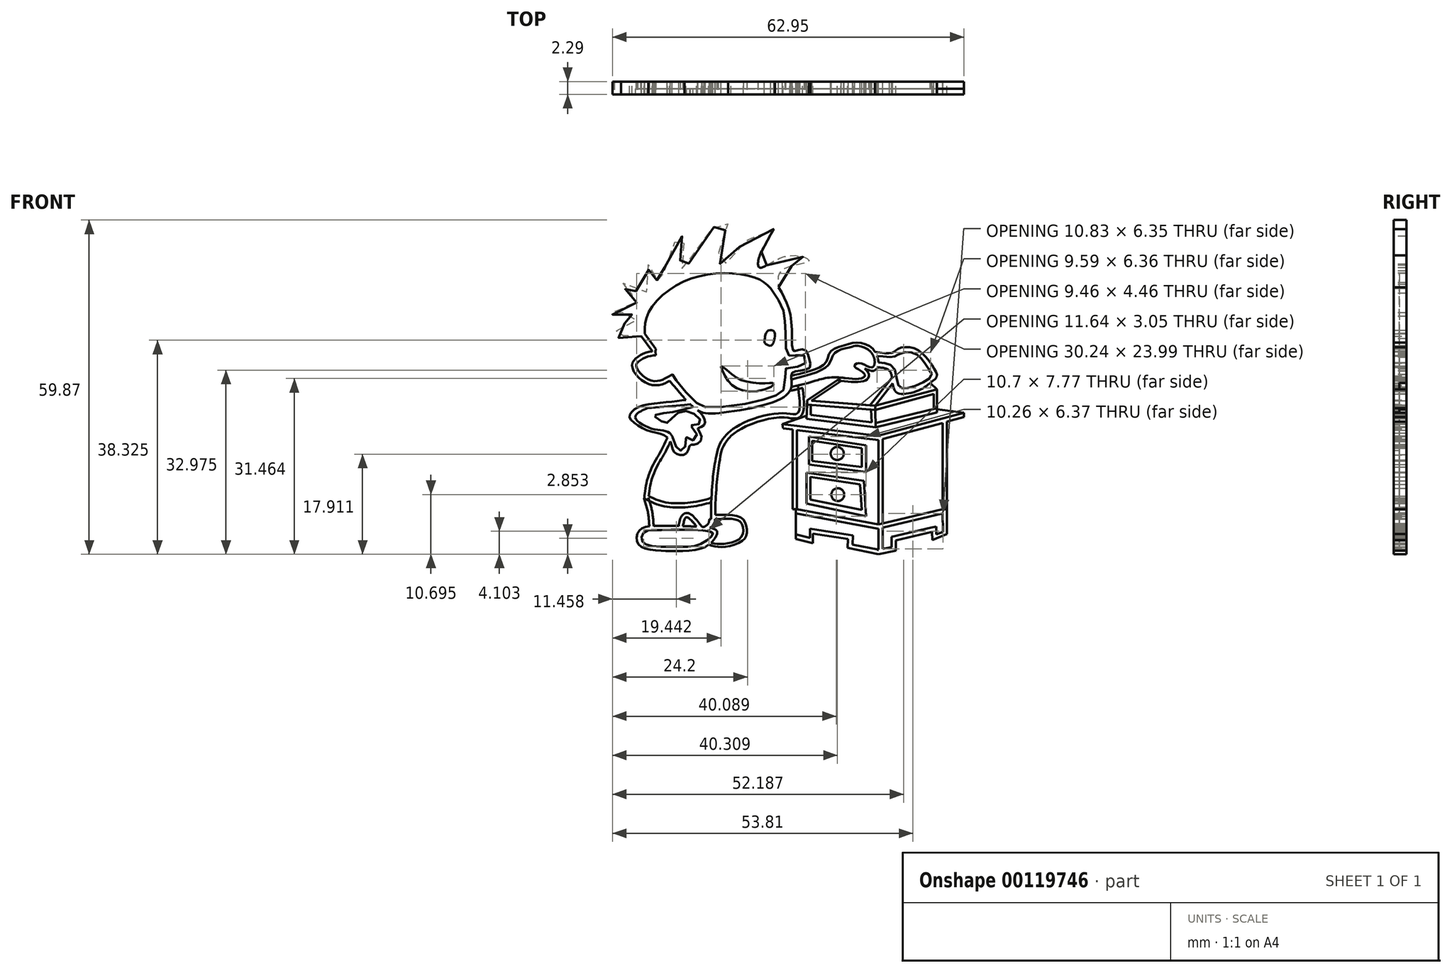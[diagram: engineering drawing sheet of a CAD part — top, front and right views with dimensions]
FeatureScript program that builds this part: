
annotation { "Feature Type Name" : "Feature", "Feature Type Description" : "" }
export const myFeature = defineFeature(function(context is Context, id is Id, definition is map)
    precondition{}
    {
        {
            var Q0;
            Q0=qCreatedBy(makeId("Front.planeOp"),FACE);
            var sketch = newSketch(context, id + "F0", { "sketchPlane" : qUnion([Q0])});
            skFitSpline(sketch, "E0", {"points": [v(200.47, 7.48) * mm, v(198.73, 7.17) * mm, v(197.12, 6.3) * mm, v(196.3, 5.12) * mm, v(196.99, 3.25) * mm, v(199.43, 1.5) * mm, v(201.65, 1.5) * mm, v(203.03, 2.15) * mm], "startDerivative": vector(-12.85, -1.34) * mm, "endDerivative": vector(9.7, 5.6) * mm});
            skFitSpline(sketch, "E1", {"points": [v(220.12, 1.68) * mm, v(216.68, 2.03) * mm, v(214.2, 3.29) * mm, v(212.24, 4.78) * mm, v(212.85, 3.16) * mm, v(214.76, 0.99) * mm, v(218.9, 0.29) * mm, v(221.69, 1.5) * mm, v(221.43, 1.73) * mm, v(220.12, 1.68) * mm]});
            skFitSpline(sketch, "E2", {"points": [v(222.53, 18.87) * mm, v(224.03, 16) * mm, v(224.88, 11.69) * mm, v(225.14, 7.57) * mm, v(225.8, 7.57) * mm, v(227.23, 7.7) * mm, v(228.08, 5.88) * mm, v(227.95, 4.38) * mm, v(225.53, 3.85) * mm, v(224.82, 3.29) * mm, v(224.82, 1.05) * mm, v(222.2, -1.43) * mm, v(211.57, -3.65) * mm, v(208.04, -3.13) * mm, v(203.03, 2.15) * mm], "startDerivative": vector(22.12, -37.26) * mm, "endDerivative": vector(-48.02, 59.15) * mm});
            skFitSpline(sketch, "E3", {"points": [v(197.92, 10.15) * mm, v(195.7, 10.54) * mm, v(193.15, 9.76) * mm, v(194.66, 12.3) * mm, v(197.27, 13.15) * mm, v(194.92, 14.33) * mm, v(192.83, 13.74) * mm, v(193.94, 15.63) * mm, v(197.79, 16.28) * mm, v(195.05, 18.57) * mm, v(194.4, 19.74) * mm, v(198.73, 17.92) * mm, v(199.22, 23) * mm, v(200.53, 20.6) * mm, v(201.5, 19.42) * mm, v(202.94, 25.49) * mm, v(205.62, 27.97) * mm, v(204.9, 23.6) * mm, v(205.75, 21.83) * mm, v(207.7, 26.14) * mm, v(213.39, 30.9) * mm, v(211.89, 26.01) * mm, v(212.4, 22.81) * mm, v(216.2, 26.8) * mm, v(221.8, 29.2) * mm, v(219.65, 25.68) * mm, v(219.13, 22.42) * mm, v(224.1, 24.5) * mm, v(227.94, 23.6) * mm, v(223.24, 22.03) * mm, v(222.53, 18.87) * mm], "startDerivative": vector(-75.72, 34.65) * mm, "endDerivative": vector(13.75, -116.93) * mm});
            skLineSegment(sketch, "E4", {"start": v(197.92, 10.15) * mm, "end": v(199.89, 7.42) * mm});
            skFitSpline(sketch, "E5", {"points": [v(221.8, 10.83) * mm, v(220.92, 11.22) * mm, v(220.23, 10.63) * mm, v(220.04, 9.66) * mm, v(220.04, 8.97) * mm, v(221.17, 8.44) * mm, v(221.7, 9.36) * mm, v(221.8, 10.83) * mm]});
            skFitSpline(sketch, "E6", {"points": [v(202.64, -8.02) * mm, v(201.53, -10.3) * mm, v(200.1, -12.85) * mm, v(198.92, -15.92) * mm, v(198.46, -18.92) * mm], "startDerivative": vector(-4.48, -9.82) * mm, "endDerivative": vector(-1.21, -11.78) * mm});
            skFitSpline(sketch, "E7", {"points": [v(213.47, -7.17) * mm, v(211.9, -9.4) * mm, v(211.12, -12.66) * mm, v(210.8, -14.94) * mm, v(210.47, -19.64) * mm], "startDerivative": vector(-7.67, -8.64) * mm, "endDerivative": vector(-0.98, -17.2) * mm});
            skFitSpline(sketch, "E8", {"points": [v(199.02, -2.78) * mm, v(197.62, -3.44) * mm, v(196.88, -4.43) * mm, v(200, -6.49) * mm, v(203.13, -7.32) * mm, v(204.37, -10.02) * mm, v(205.35, -10.27) * mm, v(206.01, -8.58) * mm, v(205.84, -7.85) * mm, v(207.01, -8.54) * mm, v(207.84, -7.33) * mm, v(206.7, -5.84) * mm, v(207.64, -5.81) * mm, v(208.57, -5.15) * mm, v(207.36, -3.77) * mm, v(205.18, -3.32) * mm, v(203.28, -4.74) * mm, v(202.38, -5.43) * mm, v(200.9, -4.67) * mm, v(200.24, -4.12) * mm, v(201.3, -3.77) * mm, v(204.21, -3.32) * mm, v(206.63, -2.71) * mm], "startDerivative": vector(-32.65, -13.12) * mm, "endDerivative": vector(42.45, 11.6) * mm});
            skFitSpline(sketch, "E9", {"points": [v(199.02, -2.78) * mm, v(205.7, -2.22) * mm], "startDerivative": vector(6.68, 0.57) * mm, "endDerivative": vector(6.68, 0.57) * mm});
            skFitSpline(sketch, "E10", {"points": [v(198.46, -18.92) * mm, v(201.8, -20.3) * mm, v(206.75, -20.42) * mm, v(210.47, -19.64) * mm], "startDerivative": vector(9.87, -5.24) * mm, "endDerivative": vector(10.91, 2.84) * mm});
            skFitSpline(sketch, "E11", {"points": [v(204.18, -23.87) * mm, v(208.54, -24.02) * mm, v(211.46, -24.76) * mm, v(210.8, -26.47) * mm, v(208.17, -28.03) * mm, v(203.48, -28.36) * mm, v(202.9, -28.34) * mm, v(199.16, -28.03) * mm, v(197.15, -26.63) * mm, v(197.7, -24.55) * mm, v(199.86, -23.89) * mm, v(204.18, -23.87) * mm]});
            skFitSpline(sketch, "E12", {"points": [v(210.13, -22.64) * mm, v(213.13, -22.59) * mm, v(215.72, -23.2) * mm, v(215.77, -25.93) * mm, v(211.8, -27.1) * mm, v(210.42, -26.88) * mm], "startDerivative": vector(13.97, 0.31) * mm, "endDerivative": vector(-7.5, 2) * mm});
            skFitSpline(sketch, "E13", {"points": [v(198.46, -18.92) * mm, v(199.14, -21.53) * mm, v(199.38, -23.92) * mm], "startDerivative": vector(1.54, -5.1) * mm, "endDerivative": vector(0.29, -4.88) * mm});
            skFitSpline(sketch, "E14", {"points": [v(205.39, -23.9) * mm, v(206.03, -22.32) * mm, v(207.83, -23.99) * mm], "startDerivative": vector(0.99, 5.02) * mm, "endDerivative": vector(3.82, -4.9) * mm});
            skFitSpline(sketch, "E15", {"points": [v(210.47, -19.64) * mm, v(210.47, -22.64) * mm], "startDerivative": vector(0, -3) * mm, "endDerivative": vector(0, -3) * mm});
            skFitSpline(sketch, "E16", {"points": [v(210.13, -22.64) * mm, v(209.9, -23.48) * mm, v(209.1, -24.06) * mm], "startDerivative": vector(-0.24, -1.87) * mm, "endDerivative": vector(-1.8, -0.98) * mm});
            skFitSpline(sketch, "E17", {"points": [v(224.82, 2.37) * mm, v(231.46, 5.01) * mm, v(232.65, 7.19) * mm, v(235.55, 8.22) * mm, v(236.33, 8.43) * mm, v(238.6, 7.7) * mm, v(239.74, 5.53) * mm, v(239.17, 4.55) * mm, v(236.9, 5.32) * mm, v(236.12, 4.8) * mm, v(237, 4.08) * mm, v(237.98, 3.1) * mm, v(236.8, 2.47) * mm, v(232.5, 2.78) * mm, v(228.97, 2.11) * mm, v(227.83, 1.75) * mm, v(224.82, 1.05) * mm], "startDerivative": vector(75.89, 18.92) * mm, "endDerivative": vector(-47.72, -10.82) * mm});
            skFitSpline(sketch, "E18", {"points": [v(226, 1.31) * mm, v(226, -3.63) * mm, v(224.47, -3.76) * mm, v(220.81, -3.9) * mm, v(215.6, -5.72) * mm, v(213.47, -7.17) * mm], "startDerivative": vector(3.4, -27.05) * mm, "endDerivative": vector(-10.35, -8.32) * mm});
            skFitSpline(sketch, "E19", {"points": [v(239.74, 7.36) * mm, v(243, 7.18) * mm, v(243.93, 7.88) * mm, v(247.13, 7.82) * mm, v(250.27, 4.55) * mm, v(250.85, 2.88) * mm, v(249.69, 1.78) * mm, v(247.88, 0.55) * mm, v(243.7, 0.03) * mm, v(242.88, 2.36) * mm, v(242.18, 4.1) * mm, v(239.17, 4.55) * mm], "startDerivative": vector(38.24, -6.3) * mm, "endDerivative": vector(-36.2, -0.09) * mm});
            skLineSegment(sketch, "E20", {"start": v(240.4, -9.29) * mm, "end": v(240.4, -23.57) * mm});
            skLineSegment(sketch, "E21", {"start": v(240.4, -23.57) * mm, "end": v(251.9, -20.86) * mm});
            skLineSegment(sketch, "E22", {"start": v(251.9, -20.86) * mm, "end": v(251.9, -6.06) * mm});
            skLineSegment(sketch, "E23", {"start": v(223.33, -6.38) * mm, "end": v(240.4, -8.5) * mm});
            skLineSegment(sketch, "E24", {"start": v(240.4, -8.5) * mm, "end": v(255.7, -4.38) * mm});
            skLineSegment(sketch, "E25", {"start": v(225.82, -7.3) * mm, "end": v(225.82, -20.86) * mm});
            skLineSegment(sketch, "E26", {"start": v(237.83, -15.8) * mm, "end": v(227.5, -14.34) * mm});
            skLineSegment(sketch, "E27", {"start": v(227.5, -14.34) * mm, "end": v(227.5, -19.84) * mm});
            skLineSegment(sketch, "E28", {"start": v(227.5, -19.84) * mm, "end": v(238.2, -22.1) * mm});
            skLineSegment(sketch, "E29", {"start": v(238.2, -22.1) * mm, "end": v(237.83, -15.8) * mm});
            skLineSegment(sketch, "E30", {"start": v(227.94, -7.82) * mm, "end": v(227.94, -12.88) * mm});
            skLineSegment(sketch, "E31", {"start": v(227.94, -12.88) * mm, "end": v(238.2, -14.2) * mm});
            skLineSegment(sketch, "E32", {"start": v(238.2, -14.2) * mm, "end": v(238.2, -9.43) * mm});
            skLineSegment(sketch, "E33", {"start": v(238.2, -9.43) * mm, "end": v(227.94, -7.82) * mm});
            skLineSegment(sketch, "E34", {"start": v(225.82, -20.86) * mm, "end": v(240.4, -23.57) * mm});
            skLineSegment(sketch, "E35", {"start": v(240.4, -23.57) * mm, "end": v(240.4, -28.92) * mm});
            skLineSegment(sketch, "E36", {"start": v(240.4, -28.92) * mm, "end": v(243.5, -28.31) * mm});
            skLineSegment(sketch, "E37", {"start": v(243.5, -28.31) * mm, "end": v(243.5, -26.45) * mm});
            skLineSegment(sketch, "E38", {"start": v(243.5, -26.45) * mm, "end": v(249.98, -24.9) * mm});
            skLineSegment(sketch, "E39", {"start": v(249.98, -24.9) * mm, "end": v(250.04, -26.4) * mm});
            skLineSegment(sketch, "E40", {"start": v(250.04, -26.4) * mm, "end": v(252.67, -25.3) * mm});
            skLineSegment(sketch, "E41", {"start": v(252.67, -25.3) * mm, "end": v(252.67, -20.85) * mm});
            skLineSegment(sketch, "E42", {"start": v(252.67, -20.85) * mm, "end": v(251.9, -20.86) * mm});
            skLineSegment(sketch, "E43", {"start": v(225.82, -20.86) * mm, "end": v(224.84, -20.86) * mm});
            skLineSegment(sketch, "E44", {"start": v(224.84, -20.86) * mm, "end": v(224.84, -25.97) * mm});
            skLineSegment(sketch, "E45", {"start": v(224.84, -25.97) * mm, "end": v(228.69, -26.95) * mm});
            skLineSegment(sketch, "E46", {"start": v(228.69, -26.95) * mm, "end": v(228.69, -24.47) * mm});
            skLineSegment(sketch, "E47", {"start": v(228.69, -24.47) * mm, "end": v(235, -25.45) * mm});
            skLineSegment(sketch, "E48", {"start": v(235, -25.45) * mm, "end": v(234.89, -27.76) * mm});
            skLineSegment(sketch, "E49", {"start": v(234.89, -27.76) * mm, "end": v(240.4, -28.92) * mm});
            skLineSegment(sketch, "E50", {"start": v(205.7, -2.22) * mm, "end": v(206.7, -2.04) * mm});
            skLineSegment(sketch, "E51", {"start": v(206.63, -2.71) * mm, "end": v(207.22, -2.52) * mm});
            skLineSegment(sketch, "E52", {"start": v(227.54, -4.64) * mm, "end": v(239.9, -6.18) * mm});
            skLineSegment(sketch, "E53", {"start": v(239.9, -6.18) * mm, "end": v(250.9, -3.55) * mm});
            skLineSegment(sketch, "E54", {"start": v(250.9, -3.55) * mm, "end": v(250.9, 0.6) * mm});
            skLineSegment(sketch, "E55", {"start": v(250.9, 0.6) * mm, "end": v(239.82, -2.3) * mm});
            skLineSegment(sketch, "E56", {"start": v(239.82, -2.3) * mm, "end": v(227.64, -1.37) * mm});
            skLineSegment(sketch, "E57", {"start": v(227.64, -1.37) * mm, "end": v(227.54, -4.64) * mm});
            skLineSegment(sketch, "E58", {"start": v(227.64, -1.37) * mm, "end": v(233.7, 2.72) * mm});
            skLineSegment(sketch, "E59", {"start": v(239.82, -2.3) * mm, "end": v(242.95, 1.67) * mm});
            skLineSegment(sketch, "E60", {"start": v(250.9, 0.6) * mm, "end": v(249.69, 1.78) * mm});
            skLineSegment(sketch, "E61", {"start": v(239.82, -2.3) * mm, "end": v(239.9, -6.18) * mm});
            skFitSpline(sketch, "E62.0", {"points": [v(200.55, 6.72) * mm, v(200.28, 6.7) * mm, v(199.9, 6.65) * mm, v(199.42, 6.57) * mm, v(199.08, 6.49) * mm, v(198.76, 6.38) * mm, v(198.43, 6.24) * mm, v(198.12, 6.07) * mm, v(197.82, 5.88) * mm, v(197.53, 5.66) * mm, v(197.3, 5.45) * mm, v(197.14, 5.26) * mm, v(197.08, 5.13) * mm, v(197.05, 5.04) * mm, v(197.04, 4.95) * mm, v(197.04, 4.79) * mm, v(197.11, 4.52) * mm, v(197.26, 4.2) * mm, v(197.48, 3.85) * mm, v(197.85, 3.4) * mm, v(198.32, 2.96) * mm, v(198.84, 2.6) * mm, v(199.24, 2.39) * mm, v(199.63, 2.23) * mm, v(200.14, 2.11) * mm, v(200.64, 2.1) * mm, v(201.12, 2.16) * mm, v(201.45, 2.24) * mm, v(201.76, 2.35) * mm, v(202.15, 2.53) * mm, v(202.45, 2.7) * mm, v(202.65, 2.81) * mm]});
            skFitSpline(sketch, "E63.0", {"points": [v(198.82, -18.25) * mm, v(199.23, -18.47) * mm, v(199.83, -18.79) * mm, v(200.65, -19.15) * mm, v(201.28, -19.38) * mm, v(201.95, -19.56) * mm, v(202.7, -19.7) * mm, v(203.49, -19.77) * mm, v(204.31, -19.8) * mm, v(205.15, -19.8) * mm, v(205.97, -19.74) * mm, v(206.77, -19.65) * mm, v(207.76, -19.5) * mm, v(208.92, -19.25) * mm, v(209.82, -19.02) * mm, v(210.28, -18.9) * mm]});
            skFitSpline(sketch, "E64.0", {"points": [v(203.33, -8.34) * mm, v(203.14, -8.75) * mm, v(202.86, -9.37) * mm, v(202.44, -10.21) * mm, v(202.1, -10.85) * mm, v(201.73, -11.48) * mm, v(201.37, -12.1) * mm, v(201, -12.74) * mm, v(200.55, -13.6) * mm, v(200.15, -14.52) * mm, v(199.83, -15.45) * mm, v(199.64, -16.15) * mm, v(199.49, -16.85) * mm, v(199.34, -17.79) * mm, v(199.27, -18.5) * mm, v(199.22, -19) * mm]});
            skFitSpline(sketch, "E65.0", {"points": [v(199.19, -18.7) * mm, v(199.32, -19.13) * mm, v(199.51, -19.78) * mm, v(199.74, -20.65) * mm, v(199.88, -21.32) * mm, v(199.99, -21.99) * mm, v(200.08, -22.85) * mm, v(200.11, -23.47) * mm, v(200.14, -23.88) * mm]});
            skFitSpline(sketch, "E66.0", {"points": [v(204.64, -23.75) * mm, v(204.66, -23.64) * mm, v(204.7, -23.43) * mm, v(204.77, -23.1) * mm, v(204.85, -22.8) * mm, v(204.95, -22.49) * mm, v(205.06, -22.24) * mm, v(205.19, -22.03) * mm, v(205.31, -21.88) * mm, v(205.49, -21.73) * mm, v(205.71, -21.6) * mm, v(206, -21.54) * mm, v(206.25, -21.55) * mm, v(206.46, -21.6) * mm, v(206.7, -21.7) * mm, v(206.95, -21.87) * mm, v(207.21, -22.09) * mm, v(207.46, -22.34) * mm, v(207.7, -22.61) * mm, v(208.03, -23) * mm, v(208.27, -23.31) * mm, v(208.43, -23.52) * mm]});
            skLineSegment(sketch, "E67", {"start": v(204.64, -23.75) * mm, "end": v(204.64, -23.88) * mm});
            skLineSegment(sketch, "E68", {"start": v(208.43, -23.52) * mm, "end": v(208.84, -24.04) * mm});
            skLineSegment(sketch, "E69", {"start": v(200.14, -23.88) * mm, "end": v(200.14, -23.88) * mm});
            skLineSegment(sketch, "E70", {"start": v(200.14, -23.88) * mm, "end": v(200.14, -23.9) * mm});
            skLineSegment(sketch, "E71", {"start": v(198.82, -18.25) * mm, "end": v(198.55, -18.08) * mm});
            skLineSegment(sketch, "E72", {"start": v(199.22, -19) * mm, "end": v(199.13, -19.28) * mm});
            skLineSegment(sketch, "E73", {"start": v(203.33, -8.34) * mm, "end": v(203.52, -7.92) * mm});
            skLineSegment(sketch, "E74", {"start": v(202.64, -8.02) * mm, "end": v(203.03, -7.22) * mm});
            skLineSegment(sketch, "E75", {"start": v(200.47, 7.48) * mm, "end": v(200.55, 6.72) * mm});
            skLineSegment(sketch, "E76", {"start": v(202.58, 2.77) * mm, "end": v(203.03, 2.15) * mm});
            skLineSegment(sketch, "E77.0", {"start": v(241.16, -9.29) * mm, "end": v(241.16, -23.57) * mm});
            skLineSegment(sketch, "E78.0", {"start": v(240.57, -24.32) * mm, "end": v(252.07, -21.6) * mm});
            skLineSegment(sketch, "E79.0", {"start": v(225.68, -21.61) * mm, "end": v(240.26, -24.32) * mm});
            skLineSegment(sketch, "E80.0", {"start": v(225.6, -20.86) * mm, "end": v(225.6, -25.95) * mm});
            skLineSegment(sketch, "E81.0", {"start": v(224.85, -25.18) * mm, "end": v(228.7, -26.17) * mm});
            skLineSegment(sketch, "E82", {"start": v(224.85, -25.18) * mm, "end": v(224.85, -25.18) * mm});
            skLineSegment(sketch, "E83", {"start": v(224.85, -25.18) * mm, "end": v(224.84, -25.18) * mm});
            skLineSegment(sketch, "E84", {"start": v(228.7, -26.17) * mm, "end": v(228.69, -26.17) * mm});
            skLineSegment(sketch, "E85", {"start": v(225.6, -25.95) * mm, "end": v(225.6, -26.16) * mm});
            skLineSegment(sketch, "E86", {"start": v(225.68, -21.61) * mm, "end": v(225.6, -21.6) * mm});
            skLineSegment(sketch, "E87", {"start": v(225.6, -21.6) * mm, "end": v(225.6, -21.6) * mm});
            skLineSegment(sketch, "E88", {"start": v(240.26, -24.32) * mm, "end": v(240.4, -24.32) * mm});
            skLineSegment(sketch, "E89", {"start": v(240.4, -24.32) * mm, "end": v(240.4, -24.39) * mm});
            skLineSegment(sketch, "E90", {"start": v(240.4, -24.32) * mm, "end": v(240.57, -24.32) * mm});
            skLineSegment(sketch, "E91", {"start": v(240.4, -9.29) * mm, "end": v(240.4, -8.5) * mm});
            skLineSegment(sketch, "E92", {"start": v(241.16, -9.29) * mm, "end": v(241.16, -8.3) * mm});
            skLineSegment(sketch, "E93", {"start": v(241.16, -23.57) * mm, "end": v(241.16, -24.18) * mm});
            skLineSegment(sketch, "E94", {"start": v(252.07, -21.6) * mm, "end": v(252.67, -21.46) * mm});
            skLineSegment(sketch, "E95.0", {"start": v(228.65, -25.23) * mm, "end": v(234.96, -26.22) * mm});
            skLineSegment(sketch, "E96", {"start": v(228.65, -25.23) * mm, "end": v(228.69, -25.26) * mm});
            skLineSegment(sketch, "E97", {"start": v(234.96, -26.22) * mm, "end": v(234.96, -26.22) * mm});
            skLineSegment(sketch, "E98", {"start": v(235.85, -25.53) * mm, "end": v(235.71, -27.94) * mm});
            skLineSegment(sketch, "E99", {"start": v(235.85, -25.53) * mm, "end": v(235, -25.45) * mm});
            skLineSegment(sketch, "E100", {"start": v(228.69, -24.47) * mm, "end": v(228.14, -24.38) * mm});
            skLineSegment(sketch, "E101", {"start": v(228.14, -24.38) * mm, "end": v(228.14, -26.81) * mm});
            skLineSegment(sketch, "E102", {"start": v(234.92, -27.06) * mm, "end": v(240.4, -28.08) * mm});
            skLineSegment(sketch, "E103", {"start": v(240.4, -28.08) * mm, "end": v(240.4, -28) * mm});
            skLineSegment(sketch, "E104.0", {"start": v(241.16, -23.57) * mm, "end": v(241.16, -28.92) * mm});
            skLineSegment(sketch, "E105", {"start": v(241.16, -28.92) * mm, "end": v(241.13, -28.77) * mm});
            skLineSegment(sketch, "E106.0", {"start": v(240.25, -28.17) * mm, "end": v(243.36, -27.56) * mm});
            skLineSegment(sketch, "E107.0", {"start": v(242.74, -28.31) * mm, "end": v(242.74, -26.45) * mm});
            skLineSegment(sketch, "E108.0", {"start": v(243.33, -25.7) * mm, "end": v(249.8, -24.17) * mm});
            skLineSegment(sketch, "E109", {"start": v(250.77, -24.72) * mm, "end": v(250.77, -26.08) * mm});
            skLineSegment(sketch, "E110", {"start": v(250.77, -24.72) * mm, "end": v(249.98, -24.9) * mm});
            skLineSegment(sketch, "E111", {"start": v(249.8, -24.17) * mm, "end": v(250.76, -23.94) * mm});
            skLineSegment(sketch, "E112", {"start": v(250.76, -23.94) * mm, "end": v(250.77, -24.72) * mm});
            skLineSegment(sketch, "E113", {"start": v(243.33, -25.7) * mm, "end": v(242.76, -25.84) * mm});
            skLineSegment(sketch, "E114", {"start": v(242.76, -25.84) * mm, "end": v(242.74, -26.45) * mm});
            skLineSegment(sketch, "E115", {"start": v(243.36, -27.56) * mm, "end": v(243.5, -27.54) * mm});
            skLineSegment(sketch, "E116", {"start": v(242.74, -28.31) * mm, "end": v(242.74, -28.46) * mm});
            skLineSegment(sketch, "E117", {"start": v(240.25, -28.17) * mm, "end": v(240.4, -28.17) * mm});
            skLineSegment(sketch, "E118.0", {"start": v(225.05, -7.3) * mm, "end": v(225.05, -20.86) * mm});
            skLineSegment(sketch, "E119.0", {"start": v(223.22, -5.6) * mm, "end": v(240.3, -7.72) * mm});
            skLineSegment(sketch, "E120", {"start": v(223.22, -5.6) * mm, "end": v(223.33, -6.38) * mm});
            skLineSegment(sketch, "E121", {"start": v(240.3, -7.72) * mm, "end": v(240.4, -8.5) * mm});
            skLineSegment(sketch, "E122", {"start": v(225.05, -7.3) * mm, "end": v(225.05, -6.6) * mm});
            skLineSegment(sketch, "E123", {"start": v(225.82, -7.3) * mm, "end": v(225.82, -6.7) * mm});
            skLineSegment(sketch, "E124", {"start": v(250.77, -25.4) * mm, "end": v(252.67, -24.7) * mm});
            skPoint(sketch, "E124.startSnap0", {"position": v(250.77, -24.33) * mm});
            skPoint(sketch, "E124.startSnap1", {"position": v(250.77, -25.4) * mm});
            skLineSegment(sketch, "E125", {"start": v(251.91, -21.64) * mm, "end": v(251.98, -24.95) * mm});
            skLineSegment(sketch, "E126.0", {"start": v(252.66, -20.86) * mm, "end": v(252.66, -6.06) * mm});
            skLineSegment(sketch, "E127", {"start": v(252.66, -20.86) * mm, "end": v(252.67, -20.85) * mm});
            skLineSegment(sketch, "E128", {"start": v(251.9, -6.06) * mm, "end": v(251.88, -5.4) * mm});
            skLineSegment(sketch, "E129", {"start": v(251.88, -5.4) * mm, "end": v(251.95, -5.4) * mm});
            skLineSegment(sketch, "E130", {"start": v(252.66, -6.06) * mm, "end": v(252.66, -5.2) * mm});
            skLineSegment(sketch, "E131", {"start": v(240.3, -7.72) * mm, "end": v(255.7, -3.57) * mm});
            skLineSegment(sketch, "E132", {"start": v(255.7, -3.57) * mm, "end": v(255.7, -4.38) * mm});
            skLineSegment(sketch, "E133", {"start": v(255.7, -3.57) * mm, "end": v(250.9, -2.97) * mm});
            skFitSpline(sketch, "E134.0", {"points": [v(214.04, -7.68) * mm, v(213.88, -7.86) * mm, v(213.57, -8.2) * mm, v(213.15, -8.73) * mm, v(212.8, -9.28) * mm, v(212.41, -10.09) * mm, v(212.15, -11.14) * mm, v(211.96, -12.2) * mm, v(211.84, -12.96) * mm, v(211.74, -13.61) * mm, v(211.65, -14.23) * mm, v(211.56, -14.89) * mm, v(211.49, -15.67) * mm, v(211.42, -16.58) * mm, v(211.33, -17.9) * mm, v(211.27, -18.97) * mm, v(211.23, -19.68) * mm]});
            skLineSegment(sketch, "E135", {"start": v(211.23, -19.68) * mm, "end": v(211.23, -22.62) * mm});
            skLineSegment(sketch, "E136", {"start": v(210.28, -18.9) * mm, "end": v(210.51, -18.85) * mm});
            skLineSegment(sketch, "E137", {"start": v(198.55, -18.08) * mm, "end": v(198.55, -18.08) * mm});
            skLineSegment(sketch, "E138", {"start": v(239.74, 7.36) * mm, "end": v(238.99, 7.36) * mm});
            skLineSegment(sketch, "E139.0", {"start": v(198.54, 10.6) * mm, "end": v(200.5, 7.86) * mm});
            skFitSpline(sketch, "E140", {"points": [v(200.5, 7.86) * mm, v(200.55, 7.78) * mm, v(200.55, 7.67) * mm, v(200.5, 7.58) * mm, v(200.47, 7.48) * mm], "startDerivative": vector(0.2, -0.33) * mm, "endDerivative": vector(-0.1, -0.4) * mm});
            skFitSpline(sketch, "E141", {"points": [v(202.58, 2.77) * mm, v(203.36, 3.28) * mm, v(203.64, 3.14) * mm, v(204.36, 2) * mm, v(207.61, -1.63) * mm, v(209.48, -2.57) * mm, v(217.5, -1.84) * mm, v(222, -0.5) * mm, v(223.38, 0.51) * mm, v(223.7, 3.62) * mm, v(224.04, 4.49) * mm, v(227.08, 4.87) * mm, v(227.33, 5.76) * mm, v(226.94, 6.8) * mm, v(225.18, 6.63) * mm, v(224.6, 6.63) * mm, v(224.07, 6.9) * mm, v(223.8, 10.57) * mm, v(223.59, 13.34) * mm, v(223.08, 15.58) * mm, v(221.1, 18.73) * mm], "startDerivative": vector(26.51, 21.37) * mm, "endDerivative": vector(-35.18, 48.62) * mm});
            skFitSpline(sketch, "E142", {"points": [v(221.1, 18.73) * mm, v(218.87, 20.38) * mm, v(212.24, 21.42) * mm, v(204.1, 19.2) * mm, v(199.13, 14.17) * mm, v(198.54, 10.6) * mm], "startDerivative": vector(-12.92, 12.56) * mm, "endDerivative": vector(-0.15, -21.4) * mm});
            skFitSpline(sketch, "E143", {"points": [v(199.87, 7.44) * mm, v(199.88, 7.43) * mm, v(199.88, 7.42) * mm, v(199.88, 7.41) * mm], "startDerivative": vector(0.01, -0.03) * mm, "endDerivative": vector(0, -0.03) * mm});
            skFitSpline(sketch, "E144", {"points": [v(200.37, -24.58) * mm, v(199.55, -24.6) * mm, v(198.29, -25.14) * mm, v(198.07, -26.52) * mm, v(199.41, -27.37) * mm, v(205.13, -27.59) * mm, v(208.47, -27.17) * mm, v(210.66, -25.52) * mm, v(210.67, -25.04) * mm, v(206.6, -24.55) * mm, v(200.37, -24.58) * mm]});
            skFitSpline(sketch, "E145", {"points": [v(211.11, -22.62) * mm, v(211.11, -23.15) * mm, v(210.69, -23.81) * mm, v(210.26, -24.2) * mm], "startDerivative": vector(0.26, -1.67) * mm, "endDerivative": vector(-1.32, -1.05) * mm});
            skFitSpline(sketch, "E146", {"points": [v(211.23, -21.9) * mm, v(213.68, -21.88) * mm, v(215.95, -22.49) * mm, v(216.76, -23.9) * mm, v(216.75, -25.45) * mm, v(215.95, -26.6) * mm, v(213.24, -27.56) * mm, v(211.39, -27.58) * mm, v(210.01, -27.23) * mm], "startDerivative": vector(16.96, 0.86) * mm, "endDerivative": vector(-12.54, 3.76) * mm});
            skFitSpline(sketch, "E147.0", {"points": [v(226.75, 1.4) * mm, v(226.78, 1.13) * mm, v(226.85, 0.56) * mm, v(226.95, -0.28) * mm, v(227.03, -1.09) * mm, v(227.07, -1.85) * mm, v(227.07, -2.55) * mm, v(227.02, -3.08) * mm, v(226.92, -3.49) * mm, v(226.8, -3.78) * mm, v(226.64, -4.07) * mm, v(226.37, -4.33) * mm, v(226.07, -4.5) * mm, v(225.77, -4.6) * mm, v(225.49, -4.62) * mm, v(225.14, -4.62) * mm, v(224.83, -4.58) * mm, v(224.53, -4.54) * mm, v(224.25, -4.5) * mm, v(223.88, -4.46) * mm, v(223.24, -4.43) * mm, v(222.39, -4.44) * mm, v(221.43, -4.55) * mm, v(220.6, -4.7) * mm, v(219.73, -4.92) * mm, v(218.6, -5.26) * mm, v(217.3, -5.75) * mm, v(216.34, -6.18) * mm, v(215.7, -6.52) * mm, v(215.16, -6.85) * mm, v(214.58, -7.26) * mm, v(214.16, -7.6) * mm, v(213.95, -7.77) * mm]});
            skLineSegment(sketch, "E148", {"start": v(226.75, 1.38) * mm, "end": v(226.75, 1.48) * mm});
            skLineSegment(sketch, "E149.0", {"start": v(227.63, -3.88) * mm, "end": v(239.9, -5.4) * mm});
            skLineSegment(sketch, "E150", {"start": v(227.63, -3.88) * mm, "end": v(227.56, -3.87) * mm});
            skLineSegment(sketch, "E151.0", {"start": v(239.76, -3.07) * mm, "end": v(227.62, -2.14) * mm});
            skLineSegment(sketch, "E152", {"start": v(239.76, -3.07) * mm, "end": v(239.84, -3.07) * mm});
            skLineSegment(sketch, "E153", {"start": v(228.27, -2.19) * mm, "end": v(228.27, -3.96) * mm});
            skLineSegment(sketch, "E154", {"start": v(228.27, -3.96) * mm, "end": v(228.22, -3.95) * mm});
            skLineSegment(sketch, "E155", {"start": v(239.09, -3.02) * mm, "end": v(239.17, -5.32) * mm});
            skLineSegment(sketch, "E156", {"start": v(239.84, -3.07) * mm, "end": v(250.9, -0.09) * mm});
            skLineSegment(sketch, "E157", {"start": v(239.9, -5.4) * mm, "end": v(250.9, -2.78) * mm});
            skLineSegment(sketch, "E158", {"start": v(250.33, -0.25) * mm, "end": v(250.33, -2.91) * mm});
            skLineSegment(sketch, "E159", {"start": v(223.22, -5.6) * mm, "end": v(227.56, -4.08) * mm});
            skLineSegment(sketch, "E160.0", {"start": v(239.22, -1.84) * mm, "end": v(242.35, 2.14) * mm});
            skFitSpline(sketch, "E161", {"points": [v(239.74, 5.53) * mm, v(241.8, 5.25) * mm, v(243.22, 4.35) * mm, v(243.97, 1.32) * mm, v(245.05, 0.77) * mm, v(247.73, 1.55) * mm, v(249.9, 3.04) * mm, v(249.47, 4.23) * mm, v(248.28, 5.92) * mm, v(246.91, 7.05) * mm, v(245.14, 7.25) * mm, v(244.53, 7.05) * mm, v(243.68, 6.7) * mm, v(243.16, 6.4) * mm, v(241.13, 6.5) * mm, v(239.5, 6.6) * mm], "startDerivative": vector(28.34, -2.82) * mm, "endDerivative": vector(-22.58, 0.84) * mm});
            skLineSegment(sketch, "E162", {"start": v(239.22, -1.84) * mm, "end": v(238.9, -2.24) * mm});
            skLineSegment(sketch, "E163", {"start": v(242.35, 2.14) * mm, "end": v(242.84, 2.73) * mm});
            skLineSegment(sketch, "E164", {"start": v(228.44, -1.44) * mm, "end": v(234.45, 2.63) * mm});
            skFitSpline(sketch, "E165", {"points": [v(224.79, 3.04) * mm, v(226.63, 3.46) * mm, v(229, 4.19) * mm, v(231.03, 5.5) * mm, v(231.76, 7.34) * mm, v(234.35, 8.53) * mm, v(236.64, 8.98) * mm, v(238.99, 8.22) * mm, v(240.04, 6.85) * mm, v(240.4, 5.62) * mm, v(240.45, 4.86) * mm, v(240, 4.17) * mm, v(239.07, 3.93) * mm, v(238, 4.3) * mm, v(238.6, 3.58) * mm, v(238.5, 2.5) * mm, v(237.36, 2.01) * mm, v(234.53, 2.04) * mm, v(232.56, 2.34) * mm, v(232.24, 2.36) * mm, v(229.95, 1.85) * mm, v(227.04, 0.94) * mm, v(224.57, 0.35) * mm], "startDerivative": vector(38.29, 7.74) * mm, "endDerivative": vector(-44.68, -8.7) * mm});
            skFitSpline(sketch, "E166", {"points": [v(205.95, -1.3) * mm, v(203.6, -1.6) * mm, v(200.03, -1.95) * mm, v(197.16, -2.71) * mm, v(195.95, -3.77) * mm, v(195.86, -4.5) * mm, v(196.95, -5.6) * mm, v(199.24, -6.85) * mm, v(201.35, -7.32) * mm, v(202.89, -8.28) * mm, v(203.45, -9.72) * mm], "startDerivative": vector(-20.1, -1.72) * mm, "endDerivative": vector(4.1, -17.97) * mm});
            skFitSpline(sketch, "E167", {"points": [v(203.45, -9.72) * mm, v(203.8, -10.52) * mm, v(204.68, -11.1) * mm, v(206.06, -10.8) * mm, v(206.69, -9.37) * mm, v(207.5, -9.3) * mm, v(208.74, -8.08) * mm, v(208.04, -6.4) * mm, v(208.28, -6.3) * mm, v(209.3, -5.58) * mm, v(209.08, -4.36) * mm, v(208.04, -3.13) * mm], "startDerivative": vector(3.1, -10.67) * mm, "endDerivative": vector(-11.62, 10.4) * mm});
            skLineSegment(sketch, "E168", {"start": v(228.25, -15.08) * mm, "end": v(228.25, -19.14) * mm});
            skPoint(sketch, "E168.startSnap0", {"position": v(232.67, -15.08) * mm});
            skLineSegment(sketch, "E169", {"start": v(228.25, -19.14) * mm, "end": v(237.4, -20.97) * mm});
            skLineSegment(sketch, "E170", {"start": v(237.4, -20.97) * mm, "end": v(237.11, -16.4) * mm});
            skLineSegment(sketch, "E171", {"start": v(237.11, -16.4) * mm, "end": v(228.25, -15.08) * mm});
            skLineSegment(sketch, "E172", {"start": v(228.52, -8.6) * mm, "end": v(228.52, -12.24) * mm});
            skLineSegment(sketch, "E173", {"start": v(228.52, -12.24) * mm, "end": v(237.42, -13.29) * mm});
            skLineSegment(sketch, "E174", {"start": v(237.42, -13.29) * mm, "end": v(237.42, -9.95) * mm});
            skLineSegment(sketch, "E175", {"start": v(237.42, -9.95) * mm, "end": v(228.52, -8.6) * mm});
            skCircle(sketch, "E176", {"center": v(233.12, -18.25) * mm, "radius": 1.15 * mm});
            skCircle(sketch, "E177", {"center": v(233.02, -10.88) * mm, "radius": 1.17 * mm});
            skSolve(sketch);
        }
        {
            var Q0;
            Q0=makeQuery(id+"F0.imprint","IMPRINT",FACE,{"disambiguationData":[TD([[makeQuery(id+"F0.imprint","IMPRINT",EDGE,{"derivedFrom":sQuery(id+"F0.wireOp",EDGE,"E1")}),-1.0]])]});
            var Q1;
            {var subQ6=sQuery(id+"F0.wireOp",EDGE,"E9");Q1=makeQuery(id+"F0.imprint","IMPRINT",FACE,{"disambiguationData":[TD([[makeQuery(id+"F0.imprint","IMPRINT",EDGE,{"derivedFrom":subQ6}),-1.0]])]});}
            var Q2;
            {var subQ0=sQuery(id+"F0.wireOp",EDGE,"E136");Q2=makeQuery(id+"F0.imprint","IMPRINT",FACE,{"disambiguationData":[TD([[makeQuery(id+"F0.imprint","IMPRINT",EDGE,{"derivedFrom":subQ0}),1.0]])]});}
            var Q3;
            {var subQ7=sQuery(id+"F0.wireOp",EDGE,"E15");Q3=makeQuery(id+"F0.imprint","IMPRINT",FACE,{"disambiguationData":[TD([[makeQuery(id+"F0.imprint","IMPRINT",EDGE,{"derivedFrom":subQ7}),-1.0]])]});}
            var Q4;
            Q4=makeQuery(id+"F0.imprint","IMPRINT",FACE,{"disambiguationData":[TD([[makeQuery(id+"F0.imprint","IMPRINT",EDGE,{"derivedFrom":sQuery(id+"F0.wireOp",EDGE,"E144")}),1.0]])]});
            var Q5;
            {var subQ0=sQuery(id+"F0.wireOp",EDGE,"E12");var subQ1=sQuery(id+"F0.wireOp",EDGE,"E11");var subQ2=makeQuery(id+"F0.imprint","INTERSECT",VERTEX,{"derivedFrom":[subQ1,subQ0]});Q5=makeQuery(id+"F0.imprint","IMPRINT",FACE,{"disambiguationData":[TD([[makeQuery(id+"F0.imprint","IMPRINT",EDGE,{"disambiguationData":[TD([[subQ2,1.0]])],"derivedFrom":subQ1}),1.0]])]});}
            var Q6;
            {var subQ1=sQuery(id+"F0.wireOp",EDGE,"E17");var subQ6=sQuery(id+"F0.wireOp",EDGE,"E2");var subQ9=makeQuery(id+"F0.imprint","INTERSECT",VERTEX,{"disambiguationData":[OD(0.0)],"derivedFrom":[subQ6,subQ1]});Q6=makeQuery(id+"F0.imprint","IMPRINT",FACE,{"disambiguationData":[TD([[makeQuery(id+"F0.imprint","IMPRINT",EDGE,{"disambiguationData":[TD([[subQ9,-1.0]])],"derivedFrom":subQ6}),1.0]])]});}
            var Q7;
            {var subQ0=sQuery(id+"F0.wireOp",EDGE,"E165");var subQ1=sQuery(id+"F0.wireOp",EDGE,"E161");var subQ2=makeQuery(id+"F0.imprint","INTERSECT",VERTEX,{"disambiguationData":[OD(0.0)],"derivedFrom":[subQ1,subQ0]});Q7=makeQuery(id+"F0.imprint","IMPRINT",FACE,{"disambiguationData":[TD([[makeQuery(id+"F0.imprint","IMPRINT",EDGE,{"disambiguationData":[TD([[subQ2,-1.0]])],"derivedFrom":subQ1}),1.0]])]});}
            var Q8;
            Q8=makeQuery(id+"F0.imprint","IMPRINT",FACE,{"disambiguationData":[TD([[makeQuery(id+"F0.imprint","IMPRINT",EDGE,{"derivedFrom":sQuery(id+"F0.wireOp",EDGE,"E160.0")}),1.0]])]});
            var Q9;
            Q9=makeQuery(id+"F0.imprint","IMPRINT",FACE,{"disambiguationData":[TD([[makeQuery(id+"F0.imprint","IMPRINT",EDGE,{"derivedFrom":sQuery(id+"F0.wireOp",EDGE,"E55")}),-1.0]])]});
            var Q10;
            {var subQ5=sQuery(id+"F0.wireOp",EDGE,"E158");Q10=makeQuery(id+"F0.imprint","IMPRINT",FACE,{"disambiguationData":[TD([[makeQuery(id+"F0.imprint","IMPRINT",EDGE,{"derivedFrom":subQ5}),-1.0]])]});}
            var Q11;
            {var subQ0=sQuery(id+"F0.wireOp",EDGE,"E153");Q11=makeQuery(id+"F0.imprint","IMPRINT",FACE,{"disambiguationData":[TD([[makeQuery(id+"F0.imprint","IMPRINT",EDGE,{"derivedFrom":subQ0}),1.0]])]});}
            var Q12;
            {var subQ1=sQuery(id+"F0.wireOp",EDGE,"E52");Q12=makeQuery(id+"F0.imprint","IMPRINT",FACE,{"disambiguationData":[TD([[makeQuery(id+"F0.imprint","IMPRINT",EDGE,{"derivedFrom":subQ1}),-1.0]])]});}
            var Q13;
            Q13=makeQuery(id+"F0.imprint","IMPRINT",FACE,{"disambiguationData":[TD([[makeQuery(id+"F0.imprint","IMPRINT",EDGE,{"derivedFrom":sQuery(id+"F0.wireOp",EDGE,"E20")}),-1.0]])]});
            var Q14;
            {var subQ6=sQuery(id+"F0.wireOp",EDGE,"E22");Q14=makeQuery(id+"F0.imprint","IMPRINT",FACE,{"disambiguationData":[TD([[makeQuery(id+"F0.imprint","IMPRINT",EDGE,{"derivedFrom":subQ6}),1.0]])]});}
            var Q15;
            Q15=makeQuery(id+"F0.imprint","IMPRINT",FACE,{"disambiguationData":[TD([[makeQuery(id+"F0.imprint","IMPRINT",EDGE,{"derivedFrom":sQuery(id+"F0.wireOp",EDGE,"E172")}),1.0]])]});
            var Q16;
            Q16=makeQuery(id+"F0.imprint","IMPRINT",FACE,{"disambiguationData":[TD([[makeQuery(id+"F0.imprint","IMPRINT",EDGE,{"derivedFrom":sQuery(id+"F0.wireOp",EDGE,"E168")}),1.0]])]});
            var Q17;
            Q17=makeQuery(id+"F0.imprint","IMPRINT",FACE,{"disambiguationData":[TD([[makeQuery(id+"F0.imprint","IMPRINT",EDGE,{"derivedFrom":sQuery(id+"F0.wireOp",EDGE,"E47")}),1.0]])]});
            var Q18;
            Q18=makeQuery(id+"F0.imprint","IMPRINT",FACE,{"disambiguationData":[TD([[makeQuery(id+"F0.imprint","IMPRINT",EDGE,{"derivedFrom":sQuery(id+"F0.wireOp",EDGE,"E108.0")}),1.0]])]});
            extrude(context, id + "F1", {"entities" : qUnion([Q0, Q1, Q2, Q3, Q4, Q5, Q6, Q7, Q8, Q9, Q10, Q11, Q12, Q13, Q14, Q15, Q16, Q17, Q18]), "depth" : 1.27 * mm});
        }
        {
            var Q0;
            {var subQ14=sQuery(id+"F0.wireOp",EDGE,"E3");Q0=makeQuery(id+"F0.imprint","IMPRINT",FACE,{"disambiguationData":[TD([[makeQuery(id+"F0.imprint","IMPRINT",EDGE,{"derivedFrom":subQ14}),-1.0]])]});}
            var Q1;
            Q1=makeQuery(id+"F0.imprint","IMPRINT",FACE,{"disambiguationData":[TD([[makeQuery(id+"F0.imprint","IMPRINT",EDGE,{"derivedFrom":sQuery(id+"F0.wireOp",EDGE,"E1")}),1.0]])]});
            var Q2;
            Q2=makeQuery(id+"F0.imprint","IMPRINT",FACE,{"disambiguationData":[TD([[makeQuery(id+"F0.imprint","IMPRINT",EDGE,{"derivedFrom":sQuery(id+"F0.wireOp",EDGE,"E5")}),1.0]])]});
            var Q3;
            Q3=makeQuery(id+"F0.imprint","IMPRINT",FACE,{"disambiguationData":[TD([[makeQuery(id+"F0.imprint","IMPRINT",EDGE,{"derivedFrom":sQuery(id+"F0.wireOp",EDGE,"E62.0")}),-1.0]])]});
            var Q4;
            {var subQ0=sQuery(id+"F0.wireOp",EDGE,"E9");Q4=makeQuery(id+"F0.imprint","IMPRINT",FACE,{"disambiguationData":[TD([[makeQuery(id+"F0.imprint","IMPRINT",EDGE,{"derivedFrom":subQ0}),1.0]])]});}
            var Q5;
            {var subQ4=sQuery(id+"F0.wireOp",EDGE,"E51");Q5=makeQuery(id+"F0.imprint","IMPRINT",FACE,{"disambiguationData":[TD([[makeQuery(id+"F0.imprint","IMPRINT",EDGE,{"derivedFrom":subQ4}),-1.0]])]});}
            var Q6;
            {var subQ5=sQuery(id+"F0.wireOp",EDGE,"E71");Q6=makeQuery(id+"F0.imprint","IMPRINT",FACE,{"disambiguationData":[TD([[makeQuery(id+"F0.imprint","IMPRINT",EDGE,{"derivedFrom":subQ5}),-1.0]])]});}
            var Q7;
            {var subQ0=sQuery(id+"F0.wireOp",EDGE,"E73");Q7=makeQuery(id+"F0.imprint","IMPRINT",FACE,{"disambiguationData":[TD([[makeQuery(id+"F0.imprint","IMPRINT",EDGE,{"derivedFrom":subQ0}),1.0]])]});}
            var Q8;
            {var subQ5=sQuery(id+"F0.wireOp",EDGE,"E136");Q8=makeQuery(id+"F0.imprint","IMPRINT",FACE,{"disambiguationData":[TD([[makeQuery(id+"F0.imprint","IMPRINT",EDGE,{"derivedFrom":subQ5}),-1.0]])]});}
            var Q9;
            {var subQ4=sQuery(id+"F0.wireOp",EDGE,"E71");Q9=makeQuery(id+"F0.imprint","IMPRINT",FACE,{"disambiguationData":[TD([[makeQuery(id+"F0.imprint","IMPRINT",EDGE,{"derivedFrom":subQ4}),1.0]])]});}
            extrude(context, id + "F2", {"entities" : qUnion([Q0, Q1, Q2, Q3, Q4, Q5, Q6, Q7, Q8, Q9]), "depth" : 2.3 * mm});
        }
        {
            var Q0;
            {var subQ0=sQuery(id+"F0.wireOp",EDGE,"E72");Q0=makeQuery(id+"F0.imprint","IMPRINT",FACE,{"disambiguationData":[TD([[makeQuery(id+"F0.imprint","IMPRINT",EDGE,{"derivedFrom":subQ0}),1.0]])]});}
            var Q1;
            {var subQ0=sQuery(id+"F0.wireOp",EDGE,"E13");Q1=makeQuery(id+"F0.imprint","IMPRINT",FACE,{"disambiguationData":[TD([[makeQuery(id+"F0.imprint","IMPRINT",EDGE,{"derivedFrom":subQ0}),1.0]])]});}
            var Q2;
            Q2=makeQuery(id+"F0.imprint","IMPRINT",FACE,{"disambiguationData":[TD([[makeQuery(id+"F0.imprint","IMPRINT",EDGE,{"derivedFrom":sQuery(id+"F0.wireOp",EDGE,"E144")}),-1.0]])]});
            var Q3;
            {var subQ0=sQuery(id+"F0.wireOp",EDGE,"E14");Q3=makeQuery(id+"F0.imprint","IMPRINT",FACE,{"disambiguationData":[TD([[makeQuery(id+"F0.imprint","IMPRINT",EDGE,{"derivedFrom":subQ0}),1.0]])]});}
            var Q4;
            {var subQ4=sQuery(id+"F0.wireOp",EDGE,"E16");Q4=makeQuery(id+"F0.imprint","IMPRINT",FACE,{"disambiguationData":[TD([[makeQuery(id+"F0.imprint","IMPRINT",EDGE,{"derivedFrom":subQ4}),1.0]])]});}
            var Q5;
            {var subQ9=sQuery(id+"F0.wireOp",EDGE,"E15");Q5=makeQuery(id+"F0.imprint","IMPRINT",FACE,{"disambiguationData":[TD([[makeQuery(id+"F0.imprint","IMPRINT",EDGE,{"derivedFrom":subQ9}),1.0]])]});}
            var Q6;
            {var subQ3=sQuery(id+"F0.wireOp",EDGE,"E146");Q6=makeQuery(id+"F0.imprint","IMPRINT",FACE,{"disambiguationData":[TD([[makeQuery(id+"F0.imprint","IMPRINT",EDGE,{"derivedFrom":subQ3}),-1.0]])]});}
            var Q7;
            {var subQ0=sQuery(id+"F0.wireOp",EDGE,"E138");Q7=makeQuery(id+"F0.imprint","IMPRINT",FACE,{"disambiguationData":[TD([[makeQuery(id+"F0.imprint","IMPRINT",EDGE,{"derivedFrom":subQ0}),-1.0]])]});}
            var Q8;
            {var subQ0=sQuery(id+"F0.wireOp",EDGE,"E17");var subQ1=sQuery(id+"F0.wireOp",EDGE,"E2");var subQ2=makeQuery(id+"F0.imprint","INTERSECT",VERTEX,{"disambiguationData":[OD(1.0)],"derivedFrom":[subQ1,subQ0]});Q8=makeQuery(id+"F0.imprint","IMPRINT",FACE,{"disambiguationData":[TD([[makeQuery(id+"F0.imprint","IMPRINT",EDGE,{"disambiguationData":[TD([[subQ2,-1.0]])],"derivedFrom":subQ1}),1.0]])]});}
            var Q9;
            {var subQ0=sQuery(id+"F0.wireOp",EDGE,"E148");Q9=makeQuery(id+"F0.imprint","IMPRINT",FACE,{"disambiguationData":[TD([[makeQuery(id+"F0.imprint","IMPRINT",EDGE,{"derivedFrom":subQ0}),1.0]])]});}
            var Q10;
            {var subQ0=sQuery(id+"F0.wireOp",EDGE,"E148");Q10=makeQuery(id+"F0.imprint","IMPRINT",FACE,{"disambiguationData":[TD([[makeQuery(id+"F0.imprint","IMPRINT",EDGE,{"derivedFrom":subQ0}),-1.0]])]});}
            var Q11;
            {var subQ5=sQuery(id+"F0.wireOp",EDGE,"E138");Q11=makeQuery(id+"F0.imprint","IMPRINT",FACE,{"disambiguationData":[TD([[makeQuery(id+"F0.imprint","IMPRINT",EDGE,{"derivedFrom":subQ5}),1.0]])]});}
            var Q12;
            {var subQ0=sQuery(id+"F0.wireOp",EDGE,"E161");var subQ1=sQuery(id+"F0.wireOp",EDGE,"E17");var subQ2=makeQuery(id+"F0.imprint","INTERSECT",VERTEX,{"disambiguationData":[OD(0.0)],"derivedFrom":[subQ1,subQ0]});Q12=makeQuery(id+"F0.imprint","IMPRINT",FACE,{"disambiguationData":[TD([[makeQuery(id+"F0.imprint","IMPRINT",EDGE,{"disambiguationData":[TD([[subQ2,1.0]])],"derivedFrom":subQ1}),1.0]])]});}
            var Q13;
            {var subQ0=sQuery(id+"F0.wireOp",EDGE,"E19");var subQ1=sQuery(id+"F0.wireOp",EDGE,"E17");var subQ2=makeQuery(id+"F0.imprint","INTERSECT",VERTEX,{"derivedFrom":[subQ1,subQ0]});Q13=makeQuery(id+"F0.imprint","IMPRINT",FACE,{"disambiguationData":[TD([[makeQuery(id+"F0.imprint","IMPRINT",EDGE,{"disambiguationData":[TD([[subQ2,1.0]])],"derivedFrom":subQ1}),1.0]])]});}
            var Q14;
            {var subQ0=sQuery(id+"F0.wireOp",EDGE,"E19");var subQ1=sQuery(id+"F0.wireOp",EDGE,"E17");var subQ2=makeQuery(id+"F0.imprint","INTERSECT",VERTEX,{"derivedFrom":[subQ1,subQ0]});Q14=makeQuery(id+"F0.imprint","IMPRINT",FACE,{"disambiguationData":[TD([[makeQuery(id+"F0.imprint","IMPRINT",EDGE,{"disambiguationData":[TD([[subQ2,-1.0]])],"derivedFrom":subQ1}),1.0]])]});}
            var Q15;
            {var subQ0=sQuery(id+"F0.wireOp",EDGE,"E58");var subQ1=sQuery(id+"F0.wireOp",EDGE,"E17");var subQ2=makeQuery(id+"F0.imprint","INTERSECT",VERTEX,{"derivedFrom":[subQ1,subQ0]});Q15=makeQuery(id+"F0.imprint","IMPRINT",FACE,{"disambiguationData":[TD([[makeQuery(id+"F0.imprint","IMPRINT",EDGE,{"disambiguationData":[TD([[subQ2,1.0]])],"derivedFrom":subQ1}),1.0]])]});}
            var Q16;
            {var subQ0=sQuery(id+"F0.wireOp",EDGE,"E19");var subQ8=makeQuery(id+"F0.imprint","INTERSECT",VERTEX,{"derivedFrom":[subQ0,sQuery(id+"F0.wireOp",EDGE,"E60")]});Q16=makeQuery(id+"F0.imprint","IMPRINT",FACE,{"disambiguationData":[TD([[makeQuery(id+"F0.imprint","IMPRINT",EDGE,{"disambiguationData":[TD([[subQ8,1.0]])],"derivedFrom":subQ0}),-1.0]])]});}
            var Q17;
            {var subQ0=sQuery(id+"F0.wireOp",EDGE,"E59");Q17=makeQuery(id+"F0.imprint","IMPRINT",FACE,{"disambiguationData":[TD([[makeQuery(id+"F0.imprint","IMPRINT",EDGE,{"derivedFrom":subQ0}),1.0]])]});}
            var Q18;
            {var subQ4=sQuery(id+"F0.wireOp",EDGE,"E150");Q18=makeQuery(id+"F0.imprint","IMPRINT",FACE,{"disambiguationData":[TD([[makeQuery(id+"F0.imprint","IMPRINT",EDGE,{"derivedFrom":subQ4}),-1.0]])]});}
            var Q19;
            {var subQ1=sQuery(id+"F0.wireOp",EDGE,"E52");Q19=makeQuery(id+"F0.imprint","IMPRINT",FACE,{"disambiguationData":[TD([[makeQuery(id+"F0.imprint","IMPRINT",EDGE,{"derivedFrom":subQ1}),1.0]])]});}
            var Q20;
            {var subQ0=sQuery(id+"F0.wireOp",EDGE,"E152");Q20=makeQuery(id+"F0.imprint","IMPRINT",FACE,{"disambiguationData":[TD([[makeQuery(id+"F0.imprint","IMPRINT",EDGE,{"derivedFrom":subQ0}),-1.0]])]});}
            var Q21;
            {var subQ4=sQuery(id+"F0.wireOp",EDGE,"E55");Q21=makeQuery(id+"F0.imprint","IMPRINT",FACE,{"disambiguationData":[TD([[makeQuery(id+"F0.imprint","IMPRINT",EDGE,{"derivedFrom":subQ4}),1.0]])]});}
            var Q22;
            {var subQ5=sQuery(id+"F0.wireOp",EDGE,"E158");Q22=makeQuery(id+"F0.imprint","IMPRINT",FACE,{"disambiguationData":[TD([[makeQuery(id+"F0.imprint","IMPRINT",EDGE,{"derivedFrom":subQ5}),1.0]])]});}
            extrude(context, id + "F3", {"entities" : qUnion([Q0, Q1, Q2, Q3, Q4, Q5, Q6, Q7, Q8, Q9, Q10, Q11, Q12, Q13, Q14, Q15, Q16, Q17, Q18, Q19, Q20, Q21, Q22]), "depth" : 2.3 * mm});
        }
        {
            var Q0;
            {var subQ1=sQuery(id+"F0.wireOp",EDGE,"E56");var subQ3=sQuery(id+"F0.wireOp",EDGE,"E164");var subQ4=makeQuery(id+"F0.imprint","INTERSECT",VERTEX,{"derivedFrom":[subQ1,subQ3]});Q0=makeQuery(id+"F0.imprint","IMPRINT",FACE,{"disambiguationData":[TD([[makeQuery(id+"F0.imprint","IMPRINT",EDGE,{"disambiguationData":[TD([[subQ4,-1.0]])],"derivedFrom":subQ3}),1.0]])]});}
            var Q1;
            {var subQ9=sQuery(id+"F0.wireOp",EDGE,"E152");Q1=makeQuery(id+"F0.imprint","IMPRINT",FACE,{"disambiguationData":[TD([[makeQuery(id+"F0.imprint","IMPRINT",EDGE,{"derivedFrom":subQ9}),1.0]])]});}
            var Q2;
            Q2=makeQuery(id+"F0.imprint","IMPRINT",FACE,{"disambiguationData":[TD([[makeQuery(id+"F0.imprint","IMPRINT",EDGE,{"derivedFrom":sQuery(id+"F0.wireOp",EDGE,"E119.0")}),-1.0]])]});
            var Q3;
            {var subQ1=sQuery(id+"F0.wireOp",EDGE,"E53");Q3=makeQuery(id+"F0.imprint","IMPRINT",FACE,{"disambiguationData":[TD([[makeQuery(id+"F0.imprint","IMPRINT",EDGE,{"derivedFrom":subQ1}),1.0]])]});}
            var Q4;
            {var subQ5=sQuery(id+"F0.wireOp",EDGE,"E121");Q4=makeQuery(id+"F0.imprint","IMPRINT",FACE,{"disambiguationData":[TD([[makeQuery(id+"F0.imprint","IMPRINT",EDGE,{"derivedFrom":subQ5}),1.0]])]});}
            var Q5;
            {var subQ6=sQuery(id+"F0.wireOp",EDGE,"E20");Q5=makeQuery(id+"F0.imprint","IMPRINT",FACE,{"disambiguationData":[TD([[makeQuery(id+"F0.imprint","IMPRINT",EDGE,{"derivedFrom":subQ6}),1.0]])]});}
            var Q6;
            {var subQ4=sQuery(id+"F0.wireOp",EDGE,"E22");Q6=makeQuery(id+"F0.imprint","IMPRINT",FACE,{"disambiguationData":[TD([[makeQuery(id+"F0.imprint","IMPRINT",EDGE,{"derivedFrom":subQ4}),-1.0]])]});}
            var Q7;
            {var subQ3=sQuery(id+"F0.wireOp",EDGE,"E25");Q7=makeQuery(id+"F0.imprint","IMPRINT",FACE,{"disambiguationData":[TD([[makeQuery(id+"F0.imprint","IMPRINT",EDGE,{"derivedFrom":subQ3}),-1.0]])]});}
            var Q8;
            Q8=makeQuery(id+"F0.imprint","IMPRINT",FACE,{"disambiguationData":[TD([[makeQuery(id+"F0.imprint","IMPRINT",EDGE,{"derivedFrom":sQuery(id+"F0.wireOp",EDGE,"E30")}),1.0]])]});
            var Q9;
            Q9=makeQuery(id+"F0.imprint","IMPRINT",FACE,{"disambiguationData":[TD([[makeQuery(id+"F0.imprint","IMPRINT",EDGE,{"derivedFrom":sQuery(id+"F0.wireOp",EDGE,"E177")}),1.0]])]});
            var Q10;
            Q10=makeQuery(id+"F0.imprint","IMPRINT",FACE,{"disambiguationData":[TD([[makeQuery(id+"F0.imprint","IMPRINT",EDGE,{"derivedFrom":sQuery(id+"F0.wireOp",EDGE,"E26")}),1.0]])]});
            var Q11;
            Q11=makeQuery(id+"F0.imprint","IMPRINT",FACE,{"disambiguationData":[TD([[makeQuery(id+"F0.imprint","IMPRINT",EDGE,{"derivedFrom":sQuery(id+"F0.wireOp",EDGE,"E176")}),1.0]])]});
            extrude(context, id + "F4", {"entities" : qUnion([Q0, Q1, Q2, Q3, Q4, Q5, Q6, Q7, Q8, Q9, Q10, Q11]), "depth" : 2.3 * mm});
        }
        {
            var Q0;
            {var subQ1=sQuery(id+"F0.wireOp",EDGE,"E34");Q0=makeQuery(id+"F0.imprint","IMPRINT",FACE,{"disambiguationData":[TD([[makeQuery(id+"F0.imprint","IMPRINT",EDGE,{"derivedFrom":subQ1}),-1.0]])]});}
            var Q1;
            {var subQ7=sQuery(id+"F0.wireOp",EDGE,"E82");Q1=makeQuery(id+"F0.imprint","IMPRINT",FACE,{"disambiguationData":[TD([[makeQuery(id+"F0.imprint","IMPRINT",EDGE,{"derivedFrom":subQ7}),-1.0]])]});}
            var Q2;
            {var subQ0=sQuery(id+"F0.wireOp",EDGE,"E82");Q2=makeQuery(id+"F0.imprint","IMPRINT",FACE,{"disambiguationData":[TD([[makeQuery(id+"F0.imprint","IMPRINT",EDGE,{"derivedFrom":subQ0}),1.0]])]});}
            var Q3;
            {var subQ0=sQuery(id+"F0.wireOp",EDGE,"E85");Q3=makeQuery(id+"F0.imprint","IMPRINT",FACE,{"disambiguationData":[TD([[makeQuery(id+"F0.imprint","IMPRINT",EDGE,{"derivedFrom":subQ0}),1.0]])]});}
            var Q4;
            {var subQ1=sQuery(id+"F0.wireOp",EDGE,"E46");var subQ6=sQuery(id+"F0.wireOp",EDGE,"E45");var subQ7=makeQuery(id+"F0.imprint","INTERSECT",VERTEX,{"derivedFrom":[subQ6,subQ1]});Q4=makeQuery(id+"F0.imprint","IMPRINT",FACE,{"disambiguationData":[TD([[makeQuery(id+"F0.imprint","IMPRINT",EDGE,{"disambiguationData":[TD([[subQ7,1.0]])],"derivedFrom":subQ6}),1.0]])]});}
            var Q5;
            {var subQ5=sQuery(id+"F0.wireOp",EDGE,"E96");Q5=makeQuery(id+"F0.imprint","IMPRINT",FACE,{"disambiguationData":[TD([[makeQuery(id+"F0.imprint","IMPRINT",EDGE,{"derivedFrom":subQ5}),-1.0]])]});}
            var Q6;
            {var subQ0=sQuery(id+"F0.wireOp",EDGE,"E47");Q6=makeQuery(id+"F0.imprint","IMPRINT",FACE,{"disambiguationData":[TD([[makeQuery(id+"F0.imprint","IMPRINT",EDGE,{"derivedFrom":subQ0}),-1.0]])]});}
            var Q7;
            {var subQ0=sQuery(id+"F0.wireOp",EDGE,"E97");Q7=makeQuery(id+"F0.imprint","IMPRINT",FACE,{"disambiguationData":[TD([[makeQuery(id+"F0.imprint","IMPRINT",EDGE,{"derivedFrom":subQ0}),1.0]])]});}
            var Q8;
            {var subQ0=sQuery(id+"F0.wireOp",EDGE,"E49");var subQ1=sQuery(id+"F0.wireOp",EDGE,"E48");var subQ2=makeQuery(id+"F0.imprint","INTERSECT",VERTEX,{"derivedFrom":[subQ1,subQ0]});Q8=makeQuery(id+"F0.imprint","IMPRINT",FACE,{"disambiguationData":[TD([[makeQuery(id+"F0.imprint","IMPRINT",EDGE,{"disambiguationData":[TD([[subQ2,1.0]])],"derivedFrom":subQ1}),1.0]])]});}
            var Q9;
            {var subQ8=sQuery(id+"F0.wireOp",EDGE,"E117");Q9=makeQuery(id+"F0.imprint","IMPRINT",FACE,{"disambiguationData":[TD([[makeQuery(id+"F0.imprint","IMPRINT",EDGE,{"derivedFrom":subQ8}),-1.0]])]});}
            var Q10;
            {var subQ5=sQuery(id+"F0.wireOp",EDGE,"E35");var subQ9=makeQuery(id+"F0.imprint","INTERSECT",VERTEX,{"derivedFrom":[subQ5,sQuery(id+"F0.wireOp",EDGE,"E117")]});Q10=makeQuery(id+"F0.imprint","IMPRINT",FACE,{"disambiguationData":[TD([[makeQuery(id+"F0.imprint","IMPRINT",EDGE,{"disambiguationData":[TD([[subQ9,1.0]])],"derivedFrom":subQ5}),1.0]])]});}
            var Q11;
            {var subQ0=sQuery(id+"F0.wireOp",EDGE,"E90");Q11=makeQuery(id+"F0.imprint","IMPRINT",FACE,{"disambiguationData":[TD([[makeQuery(id+"F0.imprint","IMPRINT",EDGE,{"derivedFrom":subQ0}),-1.0]])]});}
            var Q12;
            {var subQ0=sQuery(id+"F0.wireOp",EDGE,"E90");Q12=makeQuery(id+"F0.imprint","IMPRINT",FACE,{"disambiguationData":[TD([[makeQuery(id+"F0.imprint","IMPRINT",EDGE,{"derivedFrom":subQ0}),1.0]])]});}
            var Q13;
            {var subQ11=sQuery(id+"F0.wireOp",EDGE,"E94");Q13=makeQuery(id+"F0.imprint","IMPRINT",FACE,{"disambiguationData":[TD([[makeQuery(id+"F0.imprint","IMPRINT",EDGE,{"derivedFrom":subQ11}),1.0]])]});}
            var Q14;
            {var subQ0=sQuery(id+"F0.wireOp",EDGE,"E116");Q14=makeQuery(id+"F0.imprint","IMPRINT",FACE,{"disambiguationData":[TD([[makeQuery(id+"F0.imprint","IMPRINT",EDGE,{"derivedFrom":subQ0}),-1.0]])]});}
            var Q15;
            {var subQ4=sQuery(id+"F0.wireOp",EDGE,"E115");Q15=makeQuery(id+"F0.imprint","IMPRINT",FACE,{"disambiguationData":[TD([[makeQuery(id+"F0.imprint","IMPRINT",EDGE,{"derivedFrom":subQ4}),-1.0]])]});}
            var Q16;
            {var subQ5=sQuery(id+"F0.wireOp",EDGE,"E38");Q16=makeQuery(id+"F0.imprint","IMPRINT",FACE,{"disambiguationData":[TD([[makeQuery(id+"F0.imprint","IMPRINT",EDGE,{"derivedFrom":subQ5}),1.0]])]});}
            var Q17;
            {var subQ4=sQuery(id+"F0.wireOp",EDGE,"E39");Q17=makeQuery(id+"F0.imprint","IMPRINT",FACE,{"disambiguationData":[TD([[makeQuery(id+"F0.imprint","IMPRINT",EDGE,{"derivedFrom":subQ4}),1.0]])]});}
            var Q18;
            {var subQ4=sQuery(id+"F0.wireOp",EDGE,"E40");var subQ6=sQuery(id+"F0.wireOp",EDGE,"E41");var subQ7=makeQuery(id+"F0.imprint","INTERSECT",VERTEX,{"derivedFrom":[subQ4,subQ6]});Q18=makeQuery(id+"F0.imprint","IMPRINT",FACE,{"disambiguationData":[TD([[makeQuery(id+"F0.imprint","IMPRINT",EDGE,{"disambiguationData":[TD([[subQ7,1.0]])],"derivedFrom":subQ4}),1.0]])]});}
            var Q19;
            {var subQ4=sQuery(id+"F0.wireOp",EDGE,"E94");Q19=makeQuery(id+"F0.imprint","IMPRINT",FACE,{"disambiguationData":[TD([[makeQuery(id+"F0.imprint","IMPRINT",EDGE,{"derivedFrom":subQ4}),-1.0]])]});}
            extrude(context, id + "F5", {"entities" : qUnion([Q0, Q1, Q2, Q3, Q4, Q5, Q6, Q7, Q8, Q9, Q10, Q11, Q12, Q13, Q14, Q15, Q16, Q17, Q18, Q19]), "depth" : 2.3 * mm});
        }
        {
            var Q0;
            Q0=makeQuery(id+"F1.opExtrude","SWEPT_BODY",BODY,{"disambiguationData":[OSD([sQuery(id+"F0.wireOp",EDGE,"E2"),sQuery(id+"F0.wireOp",EDGE,"E8"),sQuery(id+"F0.wireOp",EDGE,"E9"),sQuery(id+"F0.wireOp",EDGE,"E50"),sQuery(id+"F0.wireOp",EDGE,"E51")])]});
            var Q1;
            Q1=makeQuery(id+"F1.opExtrude","SWEPT_BODY",BODY,{"disambiguationData":[OSD([sQuery(id+"F0.wireOp",EDGE,"E11"),sQuery(id+"F0.wireOp",EDGE,"E12"),sQuery(id+"F0.wireOp",EDGE,"E145")])]});
            var Q2;
            Q2=makeQuery(id+"F1.opExtrude","SWEPT_BODY",BODY,{"disambiguationData":[OSD([sQuery(id+"F0.wireOp",EDGE,"E19"),sQuery(id+"F0.wireOp",EDGE,"E55"),sQuery(id+"F0.wireOp",EDGE,"E59"),sQuery(id+"F0.wireOp",EDGE,"E60")])]});
            var Q3;
            Q3=makeQuery(id+"F1.opExtrude","SWEPT_BODY",BODY,{"disambiguationData":[OSD([sQuery(id+"F0.wireOp",EDGE,"E19"),sQuery(id+"F0.wireOp",EDGE,"E56"),sQuery(id+"F0.wireOp",EDGE,"E160.0"),sQuery(id+"F0.wireOp",EDGE,"E162"),sQuery(id+"F0.wireOp",EDGE,"E163"),sQuery(id+"F0.wireOp",EDGE,"E164"),sQuery(id+"F0.wireOp",EDGE,"E165")])]});
            var Q4;
            Q4=makeQuery(id+"F1.opExtrude","SWEPT_BODY",BODY,{"disambiguationData":[OSD([sQuery(id+"F0.wireOp",EDGE,"E144")])]});
            var Q5;
            Q5=makeQuery(id+"F1.opExtrude","SWEPT_BODY",BODY,{"disambiguationData":[OSD([sQuery(id+"F0.wireOp",EDGE,"E161"),sQuery(id+"F0.wireOp",EDGE,"E165")])]});
            var Q6;
            Q6=makeQuery(id+"F2.opExtrude","SWEPT_BODY",BODY,{"disambiguationData":[OSD([sQuery(id+"F0.wireOp",EDGE,"E0"),sQuery(id+"F0.wireOp",EDGE,"E2"),sQuery(id+"F0.wireOp",EDGE,"E3"),sQuery(id+"F0.wireOp",EDGE,"E4"),sQuery(id+"F0.wireOp",EDGE,"E6"),sQuery(id+"F0.wireOp",EDGE,"E7"),sQuery(id+"F0.wireOp",EDGE,"E8"),sQuery(id+"F0.wireOp",EDGE,"E9"),sQuery(id+"F0.wireOp",EDGE,"E10"),sQuery(id+"F0.wireOp",EDGE,"E50"),sQuery(id+"F0.wireOp",EDGE,"E51"),sQuery(id+"F0.wireOp",EDGE,"E62.0"),sQuery(id+"F0.wireOp",EDGE,"E63.0"),sQuery(id+"F0.wireOp",EDGE,"E64.0"),sQuery(id+"F0.wireOp",EDGE,"E65.0"),sQuery(id+"F0.wireOp",EDGE,"E72"),sQuery(id+"F0.wireOp",EDGE,"E74"),sQuery(id+"F0.wireOp",EDGE,"E75"),sQuery(id+"F0.wireOp",EDGE,"E136"),sQuery(id+"F0.wireOp",EDGE,"E137"),sQuery(id+"F0.wireOp",EDGE,"E139.0"),sQuery(id+"F0.wireOp",EDGE,"E140"),sQuery(id+"F0.wireOp",EDGE,"E141"),sQuery(id+"F0.wireOp",EDGE,"E142"),sQuery(id+"F0.wireOp",EDGE,"E143"),sQuery(id+"F0.wireOp",EDGE,"E166"),sQuery(id+"F0.wireOp",EDGE,"E167")])]});
            booleanBodies(context, id + "F6", {"operationType" : BooleanOperationType.UNION, "tools" : qUnion([Q0, Q1, Q2, Q3, Q4, Q5, Q6])});
        }
    });
